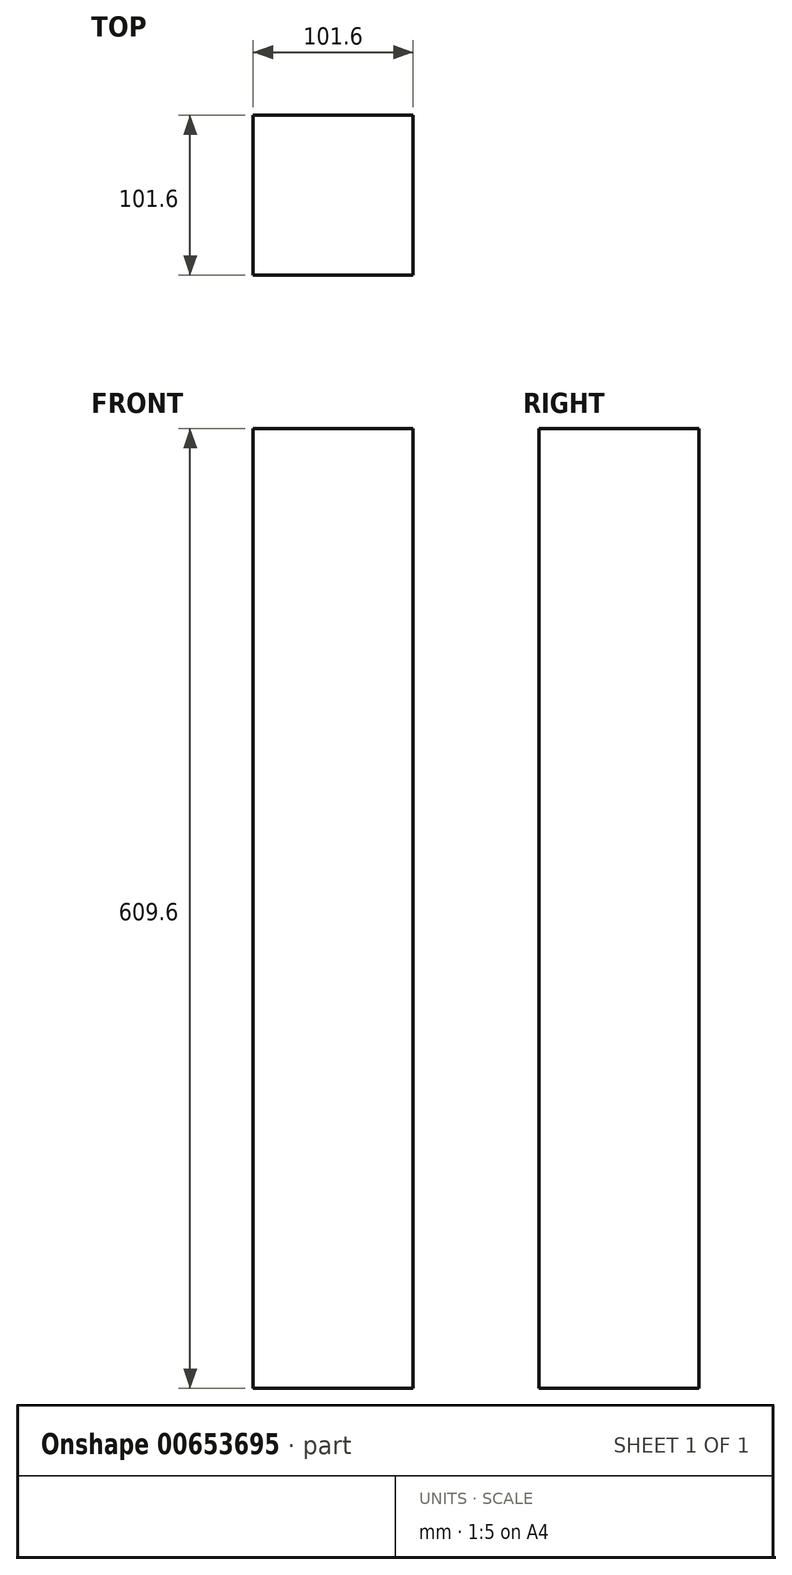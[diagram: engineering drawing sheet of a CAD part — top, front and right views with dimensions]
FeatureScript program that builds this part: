
annotation { "Feature Type Name" : "Feature", "Feature Type Description" : "" }
export const myFeature = defineFeature(function(context is Context, id is Id, definition is map)
    precondition{}
    {
        {
            var Q0;
            Q0=qCreatedBy(makeId("Top.planeOp"),FACE);
            var sketch = newSketch(context, id + "F0", { "sketchPlane" : qUnion([Q0])});
            skLineSegment(sketch, "E0.bottom", {"start": v(-127.82, 142.51) * mm, "end": v(-26.22, 142.51) * mm});
            skLineSegment(sketch, "E0.top", {"start": v(-127.82, 40.91) * mm, "end": v(-26.22, 40.91) * mm});
            skLineSegment(sketch, "E0.left", {"start": v(-127.82, 142.51) * mm, "end": v(-127.82, 40.91) * mm});
            skLineSegment(sketch, "E0.right", {"start": v(-26.22, 142.51) * mm, "end": v(-26.22, 40.91) * mm});
            skSolve(sketch);
        }
        {
            var Q0;
            Q0=makeQuery(id+"F0.imprint","IMPRINT",FACE,{"disambiguationData":[TD([[makeQuery(id+"F0.imprint","IMPRINT",EDGE,{"derivedFrom":sQuery(id+"F0.wireOp",EDGE,"E0.bottom")}),-1.0]])]});
            extrude(context, id + "F1", {"entities" : qUnion([Q0]), "oppositeDirection" : true, "depth" : 609.6 * mm, "offsetDistance" : 25.4 * mm});
        }
    });
